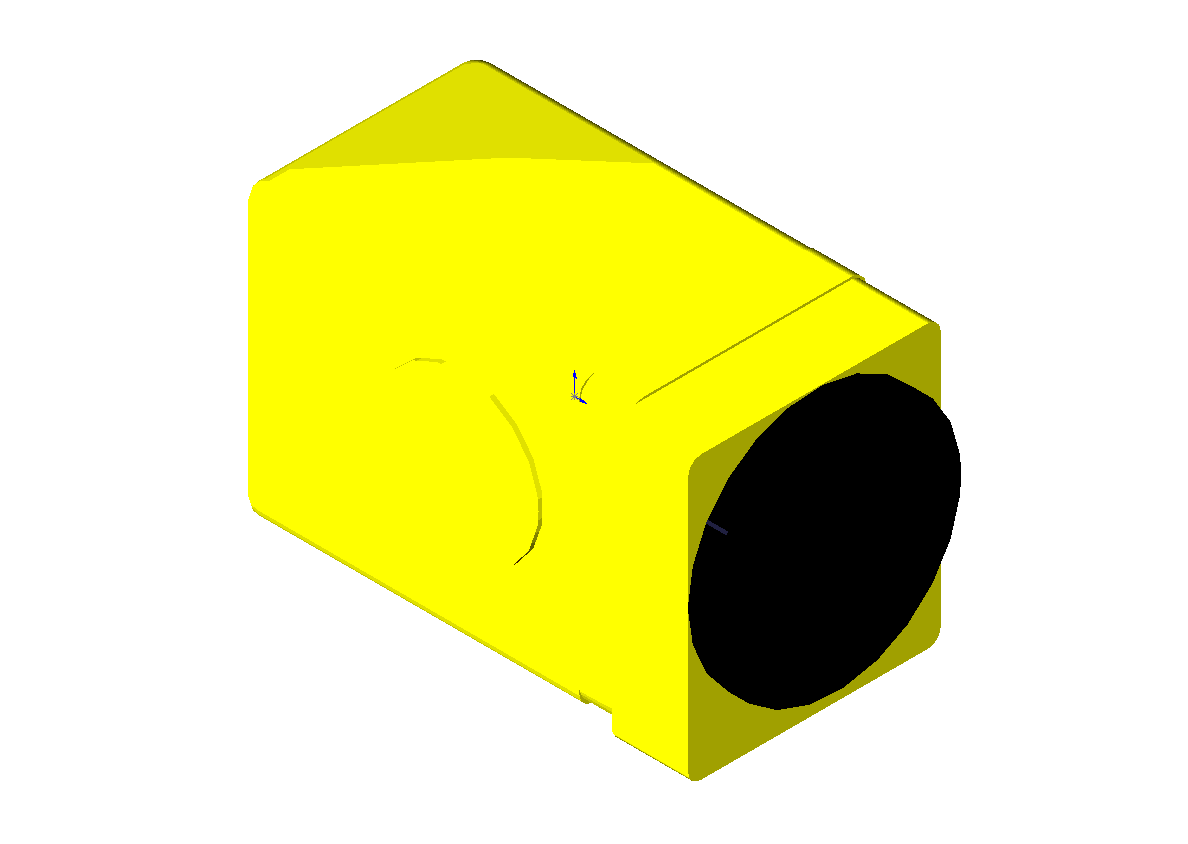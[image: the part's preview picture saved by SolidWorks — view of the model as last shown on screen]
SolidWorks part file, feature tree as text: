
SOLIDWORKS PART (.sldprt)
format: sldprt  version: not decoded by parser v0  size: 3,272,704 bytes
history: native  units: mm
features: sketch x9, extrude x6, plane x3, material x1, fillet x1 (+9 scaffold rows collapsed)
feature tree (29):
  scaffold x9  (default folders/planes/origin — collapsed)
  material  "Material <not specified>"
  plane  "FRONT"
  plane  "TOP"
  plane  "SIDE"
  sketch  "Sketch1"
  sketch  "Sketch2"
  sketch  "Sketch3"
  sketch  "Sketch4"
  extrude  "Base-Extrude"  Depth=43.18mm
  sketch  "Sketch5"  dims[D1=~54.831064mm]
  extrude  "Boss-Extrude1"  Depth=1.5875mm
  sketch  "Sketch6"
  extrude  "Boss-Extrude2"  Depth=0.89408mm
  fillet  "Fillet1"  Radius=4.826mm
  sketch  "Sketch7"  dims[D1=0.254mm]
  extrude  "Boss-Extrude3"  Depth=15.49908mm
  sketch  "Sketch8"  dims[D1=0.762mm]
  extrude  "Boss-Extrude4"  Depth=25.65908mm
  sketch  "Sketch9"
  extrude  "Boss-Extrude5"  Depth=6.92658mm
decode coverage: 10 of 16 modeling features carry decoded parameters
note: ~ marks probable driven/reference dimensions
note: suppression state not decoded; provenance and decode notes live in map.json
